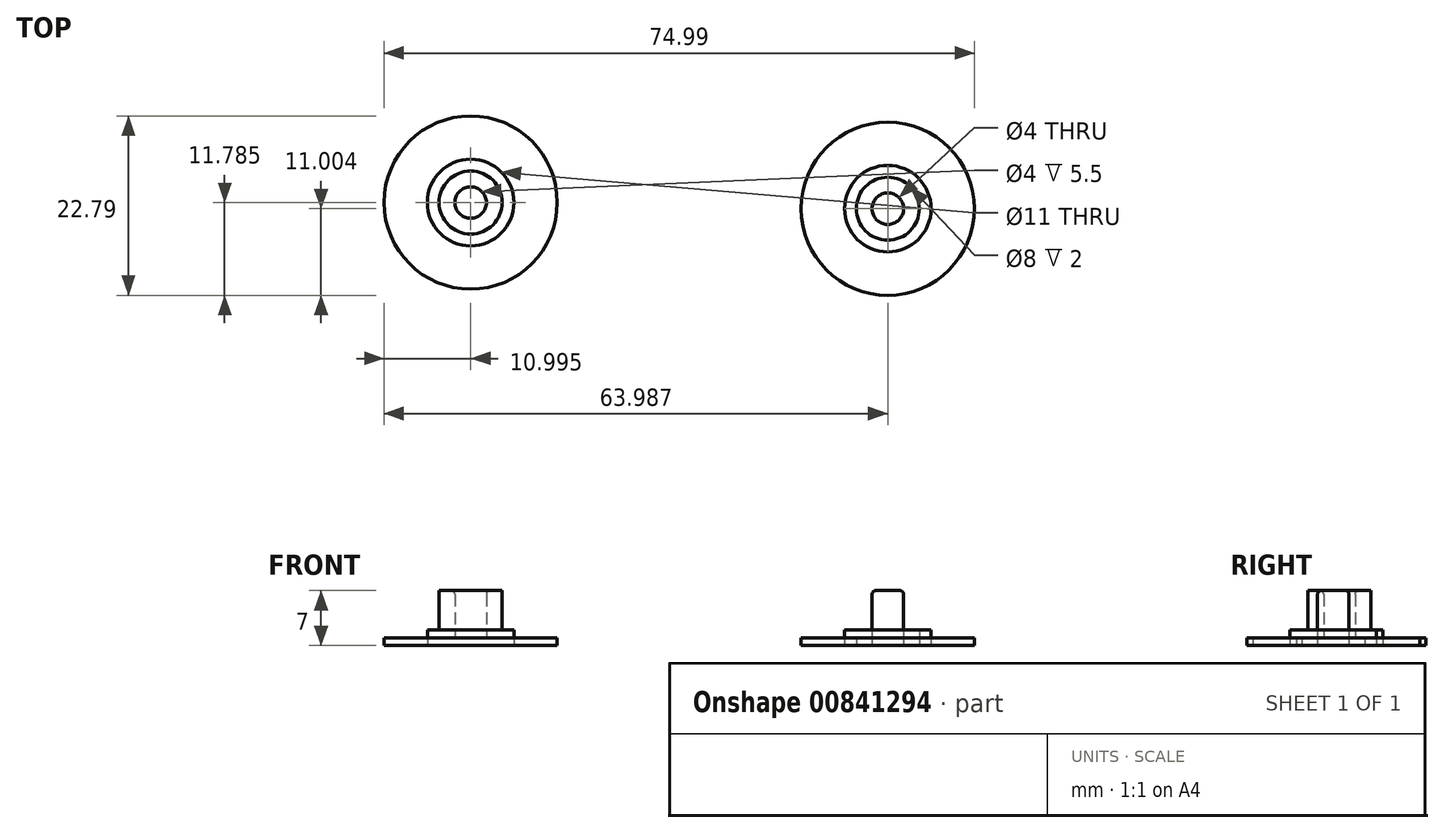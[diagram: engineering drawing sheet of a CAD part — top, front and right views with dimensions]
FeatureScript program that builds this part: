
annotation { "Feature Type Name" : "Feature", "Feature Type Description" : "" }
export const myFeature = defineFeature(function(context is Context, id is Id, definition is map)
    precondition{}
    {
        {
            var Q0;
            Q0=qCreatedBy(makeId("Top.planeOp"),FACE);
            var sketch = newSketch(context, id + "F0", { "sketchPlane" : qUnion([Q0])});
            skCircle(sketch, "E0", {"center": v(-26.73, 16.32) * mm, "radius": 11 * mm});
            skCircle(sketch, "E1", {"center": v(-26.73, 16.32) * mm, "radius": 5.5 * mm});
            skCircle(sketch, "E2", {"center": v(-26.73, 16.32) * mm, "radius": 4 * mm});
            skCircle(sketch, "E3", {"center": v(-26.73, 16.32) * mm, "radius": 2 * mm});
            skSolve(sketch);
        }
        {
            var Q0;
            Q0=makeQuery(id+"F0.imprint","IMPRINT",FACE,{"disambiguationData":[TD([[makeQuery(id+"F0.imprint","IMPRINT",EDGE,{"derivedFrom":sQuery(id+"F0.wireOp",EDGE,"E3")}),1.0]])]});
            var sketch = newSketch(context, id + "F1", { "sketchPlane" : qUnion([Q0])});
            skCircle(sketch, "E4", {"center": v(26.26, 15.53) * mm, "radius": 11 * mm});
            skCircle(sketch, "E5", {"center": v(26.26, 15.53) * mm, "radius": 5.5 * mm});
            skCircle(sketch, "E6", {"center": v(26.26, 15.53) * mm, "radius": 4 * mm});
            skCircle(sketch, "E7", {"center": v(26.26, 15.53) * mm, "radius": 2 * mm});
            skSolve(sketch);
        }
        {
            var Q0;
            Q0=makeQuery(id+"F0.imprint","IMPRINT",FACE,{"disambiguationData":[TD([[makeQuery(id+"F0.imprint","IMPRINT",EDGE,{"derivedFrom":sQuery(id+"F0.wireOp",EDGE,"E0")}),1.0]])]});
            var Q1;
            Q1=makeQuery(id+"F1.imprint","IMPRINT",FACE,{"disambiguationData":[TD([[makeQuery(id+"F1.imprint","IMPRINT",EDGE,{"derivedFrom":sQuery(id+"F1.wireOp",EDGE,"E4")}),1.0]])]});
            var Q2;
            Q2=makeQuery(id+"F1.imprint","IMPRINT",FACE,{"disambiguationData":[TD([[makeQuery(id+"F1.imprint","IMPRINT",EDGE,{"derivedFrom":sQuery(id+"F1.wireOp",EDGE,"E5")}),1.0]])]});
            var Q3;
            Q3=makeQuery(id+"F1.imprint","IMPRINT",FACE,{"disambiguationData":[TD([[makeQuery(id+"F1.imprint","IMPRINT",EDGE,{"derivedFrom":sQuery(id+"F1.wireOp",EDGE,"E6")}),1.0]])]});
            var Q4;
            Q4=makeQuery(id+"F1.imprint","IMPRINT",FACE,{"disambiguationData":[TD([[makeQuery(id+"F1.imprint","IMPRINT",EDGE,{"derivedFrom":sQuery(id+"F1.wireOp",EDGE,"E7")}),1.0]])]});
            extrude(context, id + "F2", {"entities" : qUnion([Q0, Q1, Q2, Q3, Q4]), "depth" : 1 * mm, "offsetDistance" : 25 * mm});
        }
        {
            var Q0;
            Q0=makeQuery(id+"F0.imprint","IMPRINT",FACE,{"disambiguationData":[TD([[makeQuery(id+"F0.imprint","IMPRINT",EDGE,{"derivedFrom":sQuery(id+"F0.wireOp",EDGE,"E1")}),1.0]])]});
            var Q1;
            Q1=makeQuery(id+"F1.imprint","IMPRINT",FACE,{"disambiguationData":[TD([[makeQuery(id+"F1.imprint","IMPRINT",EDGE,{"derivedFrom":sQuery(id+"F1.wireOp",EDGE,"E5")}),1.0]])]});
            extrude(context, id + "F3", {"entities" : qUnion([Q0, Q1]), "depth" : 2 * mm, "offsetDistance" : 25 * mm});
        }
        {
            var Q0;
            Q0=makeQuery(id+"F0.imprint","IMPRINT",FACE,{"disambiguationData":[TD([[makeQuery(id+"F0.imprint","IMPRINT",EDGE,{"derivedFrom":sQuery(id+"F0.wireOp",EDGE,"E2")}),1.0]])]});
            var Q1;
            Q1=makeQuery(id+"F1.imprint","IMPRINT",FACE,{"disambiguationData":[TD([[makeQuery(id+"F1.imprint","IMPRINT",EDGE,{"derivedFrom":sQuery(id+"F1.wireOp",EDGE,"E7")}),1.0]])]});
            extrude(context, id + "F4", {"entities" : qUnion([Q0, Q1]), "operationType" : NewBodyOperationType.ADD, "depth" : 7 * mm, "offsetDistance" : 25 * mm});
        }
        {
            var Q0;
            Q0=makeQuery(id+"F1.imprint","IMPRINT",FACE,{"disambiguationData":[TD([[makeQuery(id+"F1.imprint","IMPRINT",EDGE,{"derivedFrom":sQuery(id+"F1.wireOp",EDGE,"E6")}),1.0]])]});
            extrude(context, id + "F5", {"entities" : qUnion([Q0]), "depth" : 1 * mm, "offsetDistance" : 25 * mm});
        }
        {
            var Q0;
            Q0=makeQuery(id+"F0.imprint","IMPRINT",FACE,{"disambiguationData":[TD([[makeQuery(id+"F0.imprint","IMPRINT",EDGE,{"derivedFrom":sQuery(id+"F0.wireOp",EDGE,"E3")}),1.0]])]});
            extrude(context, id + "F6", {"entities" : qUnion([Q0]), "operationType" : NewBodyOperationType.ADD, "depth" : 1 * mm, "offsetDistance" : 25 * mm});
        }
        {
            var Q0;
            Q0=makeQuery(id+"F4.opExtrude","CAP_EDGE",EDGE,{"disambiguationData":[OSD([sQuery(id+"F0.wireOp",EDGE,"E3")])],"isStart":false});
            var Q1;
            Q1=makeQuery(id+"F4.opExtrude","CAP_EDGE",EDGE,{"disambiguationData":[OSD([sQuery(id+"F1.wireOp",EDGE,"E7")])],"isStart":false});
            fillet(context, id + "F7", {"entities" : qUnion([Q0, Q1]), "radius" : .5 * mm, "tangentPropagation" : true, "allowEdgeOverflow" : false});
        }
    });
